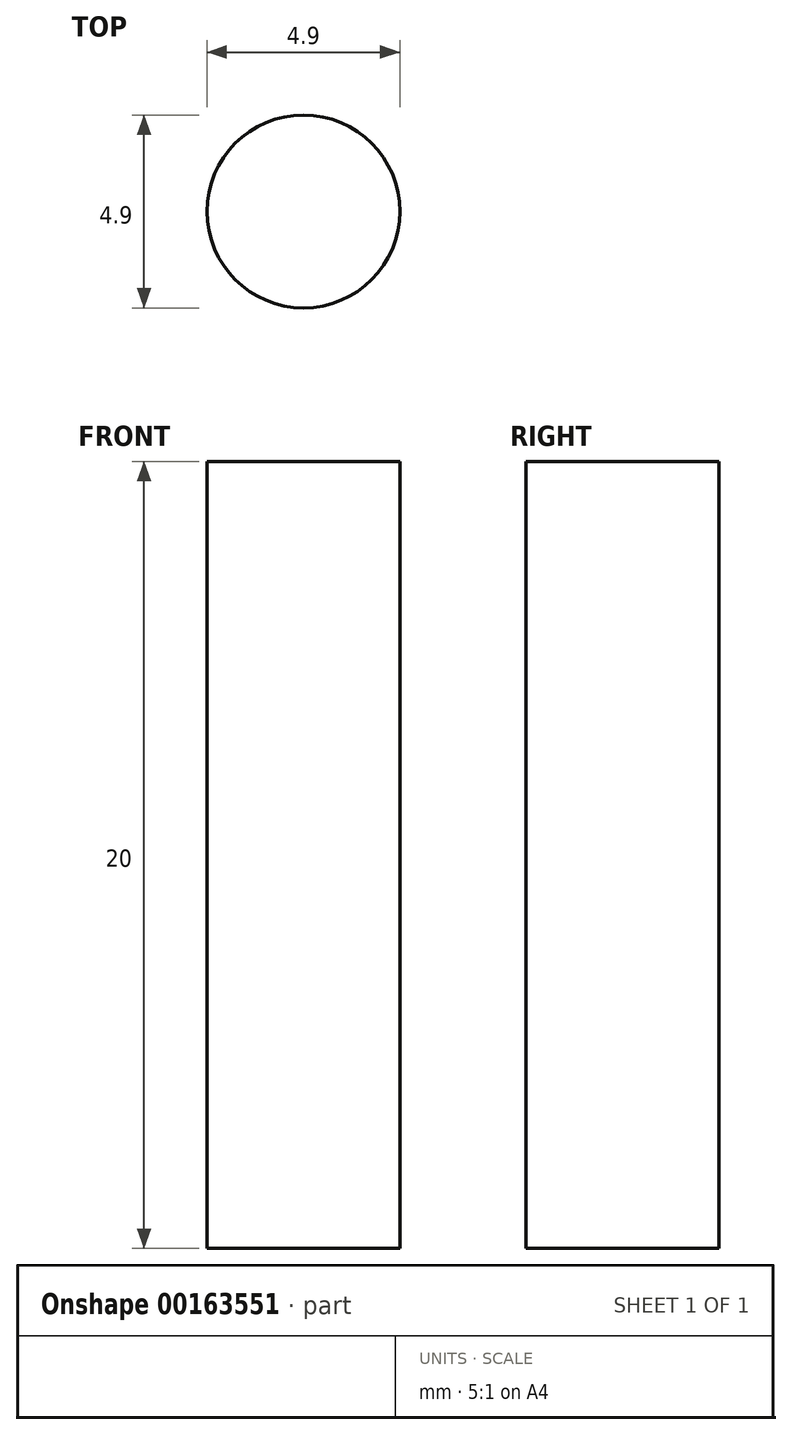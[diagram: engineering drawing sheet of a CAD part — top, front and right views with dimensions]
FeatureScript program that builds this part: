
annotation { "Feature Type Name" : "Feature", "Feature Type Description" : "" }
export const myFeature = defineFeature(function(context is Context, id is Id, definition is map)
    precondition{}
    {
        {
            var Q0;
            Q0=qCreatedBy(makeId("Top.planeOp"),FACE);
            var sketch = newSketch(context, id + "F0", { "sketchPlane" : qUnion([Q0])});
            skCircle(sketch, "E0", {"center": v(0, 0) * mm, "radius": 2.45 * mm});
            skSolve(sketch);
        }
        {
            var Q0;
            Q0=qSketchRegion(id+"F0",true);
            extrude(context, id + "F1", {"entities" : qUnion([Q0]), "depth" : 20 * mm});
        }
    });
